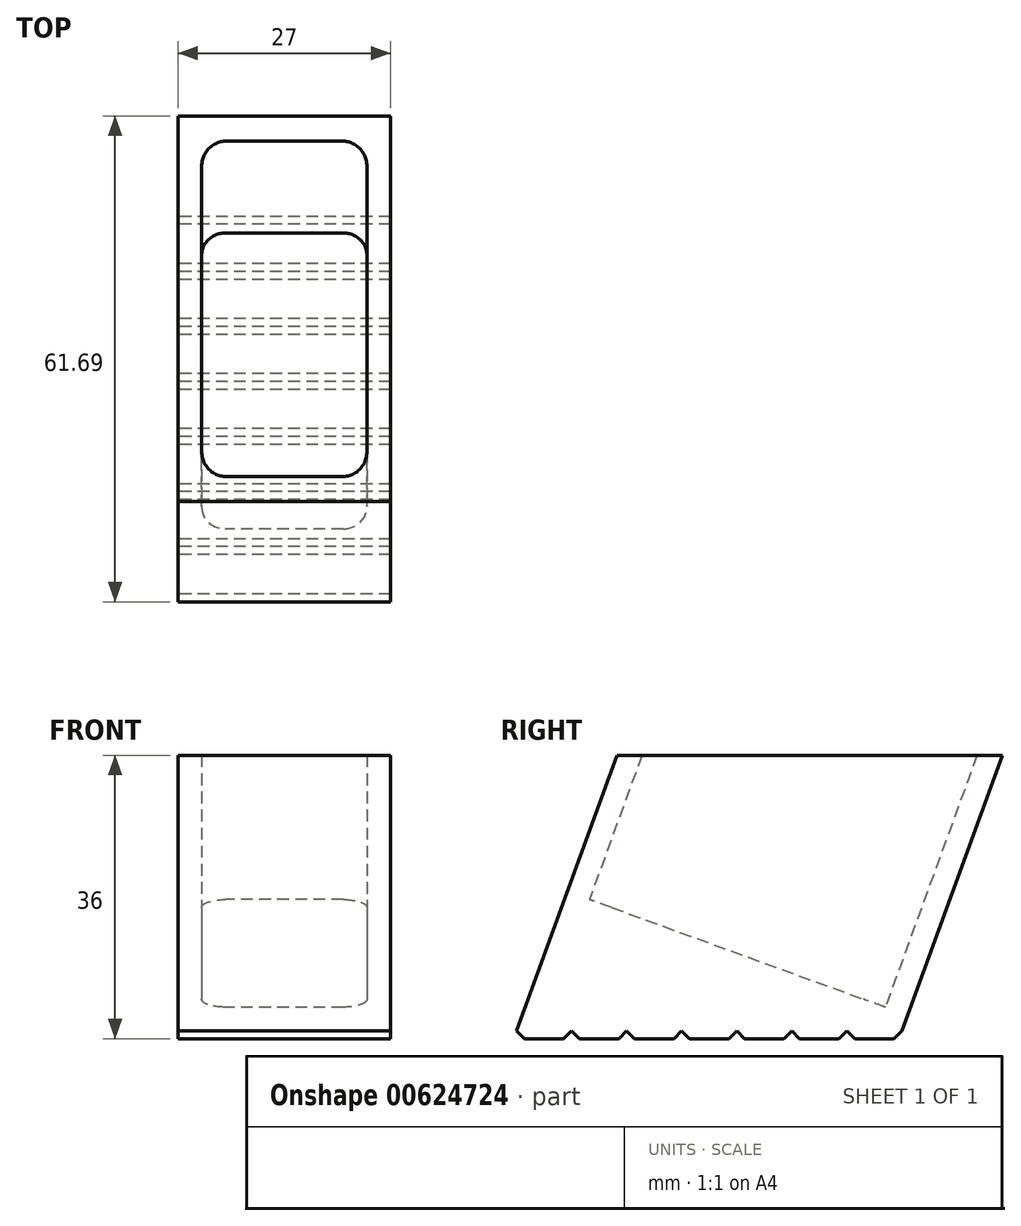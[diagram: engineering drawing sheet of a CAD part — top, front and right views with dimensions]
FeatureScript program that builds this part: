
annotation { "Feature Type Name" : "Feature", "Feature Type Description" : "" }
export const myFeature = defineFeature(function(context is Context, id is Id, definition is map)
    precondition{}
    {
        {
            var Q0;
            Q0=qCreatedBy(makeId("Right.planeOp"),FACE);
            var sketch = newSketch(context, id + "F0", { "sketchPlane" : qUnion([Q0])});
            skLineSegment(sketch, "E0", {"start": v(58.5, 35) * mm, "end": v(46.85, 3) * mm});
            skLineSegment(sketch, "E1", {"start": v(61.7, 35) * mm, "end": v(50.04, 3) * mm});
            skLineSegment(sketch, "E2", {"start": v(15.93, 35) * mm, "end": v(4.28, 3) * mm});
            skLineSegment(sketch, "E3", {"start": v(12.74, 35) * mm, "end": v(1.1, 3) * mm});
            skLineSegment(sketch, "E4", {"start": v(4.28, 3) * mm, "end": v(46.85, 3) * mm});
            skLineSegment(sketch, "E5", {"start": v(50.04, 3) * mm, "end": v(48.95, 0) * mm});
            skLineSegment(sketch, "E6", {"start": v(1.1, 3) * mm, "end": v(0, 0) * mm});
            skLineSegment(sketch, "E7", {"start": v(48.95, 0) * mm, "end": v(0, 0) * mm});
            skLineSegment(sketch, "E8", {"start": v(12.74, 35) * mm, "end": v(15.93, 35) * mm});
            skLineSegment(sketch, "E9", {"start": v(58.5, 35) * mm, "end": v(61.7, 35) * mm});
            skLineSegment(sketch, "E10", {"start": v(9.26, 16.68) * mm, "end": v(46.85, 3) * mm});
            skLineSegment(sketch, "E11", {"start": v(15.93, 35) * mm, "end": v(58.5, 35) * mm});
            skLineSegment(sketch, "E12", {"start": v(0, 0) * mm, "end": v(1, -1) * mm});
            skLineSegment(sketch, "E13", {"start": v(1, -1) * mm, "end": v(6, -1) * mm});
            skLineSegment(sketch, "E14", {"start": v(6, -1) * mm, "end": v(7, 0) * mm});
            skLineSegment(sketch, "E15.1.0.0", {"start": v(7, 0) * mm, "end": v(8, -1) * mm});
            skLineSegment(sketch, "E15.1.0.1", {"start": v(12.99, -1) * mm, "end": v(13.99, 0) * mm});
            skLineSegment(sketch, "E15.1.0.2", {"start": v(8, -1) * mm, "end": v(12.99, -1) * mm});
            skLineSegment(sketch, "E15.2.0.0", {"start": v(13.99, 0) * mm, "end": v(14.99, -1) * mm});
            skLineSegment(sketch, "E15.2.0.1", {"start": v(19.98, -1) * mm, "end": v(20.98, 0) * mm});
            skLineSegment(sketch, "E15.2.0.2", {"start": v(14.99, -1) * mm, "end": v(19.98, -1) * mm});
            skLineSegment(sketch, "E15.3.0.0", {"start": v(20.98, 0) * mm, "end": v(21.98, -1) * mm});
            skLineSegment(sketch, "E15.3.0.1", {"start": v(26.97, -1) * mm, "end": v(27.97, 0) * mm});
            skLineSegment(sketch, "E15.3.0.2", {"start": v(21.98, -1) * mm, "end": v(26.97, -1) * mm});
            skLineSegment(sketch, "E15.4.0.0", {"start": v(27.97, 0) * mm, "end": v(28.97, -1) * mm});
            skLineSegment(sketch, "E15.4.0.1", {"start": v(33.97, -1) * mm, "end": v(34.97, 0) * mm});
            skLineSegment(sketch, "E15.4.0.2", {"start": v(28.97, -1) * mm, "end": v(33.97, -1) * mm});
            skLineSegment(sketch, "E15.5.0.0", {"start": v(34.97, 0) * mm, "end": v(35.97, -1) * mm});
            skLineSegment(sketch, "E15.5.0.1", {"start": v(40.96, -1) * mm, "end": v(41.96, 0) * mm});
            skLineSegment(sketch, "E15.5.0.2", {"start": v(35.97, -1) * mm, "end": v(40.96, -1) * mm});
            skLineSegment(sketch, "E15.6.0.0", {"start": v(41.96, 0) * mm, "end": v(42.96, -1) * mm});
            skLineSegment(sketch, "E15.6.0.1", {"start": v(47.95, -1) * mm, "end": v(48.95, 0) * mm});
            skLineSegment(sketch, "E15.6.0.2", {"start": v(42.96, -1) * mm, "end": v(47.95, -1) * mm});
            skLineSegment(sketch, "E15.direction1", {"start": v(1, -1) * mm, "end": v(8, -1) * mm, "construction": true});
            skSolve(sketch);
        }
        {
            var Q0;
            Q0=makeQuery(id+"F0.imprint","IMPRINT",FACE,{"disambiguationData":[TD([[makeQuery(id+"F0.imprint","IMPRINT",EDGE,{"derivedFrom":sQuery(id+"F0.wireOp",EDGE,"E0")}),1.0]])]});
            var Q1;
            {var subQ0=sQuery(id+"F0.wireOp",EDGE,"E4");Q1=makeQuery(id+"F0.imprint","IMPRINT",FACE,{"disambiguationData":[TD([[makeQuery(id+"F0.imprint","IMPRINT",EDGE,{"derivedFrom":subQ0}),1.0]])]});}
            var Q2;
            Q2=makeQuery(id+"F0.imprint","IMPRINT",FACE,{"disambiguationData":[TD([[makeQuery(id+"F0.imprint","IMPRINT",EDGE,{"derivedFrom":sQuery(id+"F0.wireOp",EDGE,"E0")}),-1.0]])]});
            var Q3;
            {var subQ0=sQuery(id+"F0.wireOp",EDGE,"E12");Q3=makeQuery(id+"F0.imprint","IMPRINT",FACE,{"disambiguationData":[TD([[makeQuery(id+"F0.imprint","IMPRINT",EDGE,{"derivedFrom":subQ0}),1.0]])]});}
            var Q4;
            {var subQ0=sQuery(id+"F0.wireOp",EDGE,"E15.1.0.0");Q4=makeQuery(id+"F0.imprint","IMPRINT",FACE,{"disambiguationData":[TD([[makeQuery(id+"F0.imprint","IMPRINT",EDGE,{"derivedFrom":subQ0}),1.0]])]});}
            var Q5;
            {var subQ0=sQuery(id+"F0.wireOp",EDGE,"E15.2.0.0");Q5=makeQuery(id+"F0.imprint","IMPRINT",FACE,{"disambiguationData":[TD([[makeQuery(id+"F0.imprint","IMPRINT",EDGE,{"derivedFrom":subQ0}),1.0]])]});}
            var Q6;
            {var subQ0=sQuery(id+"F0.wireOp",EDGE,"E15.3.0.0");Q6=makeQuery(id+"F0.imprint","IMPRINT",FACE,{"disambiguationData":[TD([[makeQuery(id+"F0.imprint","IMPRINT",EDGE,{"derivedFrom":subQ0}),1.0]])]});}
            var Q7;
            {var subQ0=sQuery(id+"F0.wireOp",EDGE,"E15.4.0.0");Q7=makeQuery(id+"F0.imprint","IMPRINT",FACE,{"disambiguationData":[TD([[makeQuery(id+"F0.imprint","IMPRINT",EDGE,{"derivedFrom":subQ0}),1.0]])]});}
            var Q8;
            {var subQ0=sQuery(id+"F0.wireOp",EDGE,"E15.5.0.0");Q8=makeQuery(id+"F0.imprint","IMPRINT",FACE,{"disambiguationData":[TD([[makeQuery(id+"F0.imprint","IMPRINT",EDGE,{"derivedFrom":subQ0}),1.0]])]});}
            var Q9;
            {var subQ0=sQuery(id+"F0.wireOp",EDGE,"E15.6.0.0");Q9=makeQuery(id+"F0.imprint","IMPRINT",FACE,{"disambiguationData":[TD([[makeQuery(id+"F0.imprint","IMPRINT",EDGE,{"derivedFrom":subQ0}),1.0]])]});}
            extrude(context, id + "F1", {"entities" : qUnion([Q0, Q1, Q2, Q3, Q4, Q5, Q6, Q7, Q8, Q9]), "depth" : 27 * mm, "offsetDistance" : 25 * mm});
        }
        {
            var Q0;
            Q0=makeQuery(id+"F0.imprint","IMPRINT",FACE,{"disambiguationData":[TD([[makeQuery(id+"F0.imprint","IMPRINT",EDGE,{"derivedFrom":sQuery(id+"F0.wireOp",EDGE,"E0")}),-1.0]])]});
            extrude(context, id + "F2", {"entities" : qUnion([Q0]), "operationType" : NewBodyOperationType.REMOVE, "depth" : 24 * mm, "offsetDistance" : 25 * mm, "hasSecondDirection" : true, "secondDirectionOppositeDirection" : false, "secondDirectionDepth" : 3 * mm});
        }
        {
            var Q0;
            Q0=makeQuery(id+"F2.boolean.opBoolean","COPY",EDGE,{"derivedFrom":makeQuery(id+"F2.opExtrude","CAP_EDGE",EDGE,{"disambiguationData":[OSD([sQuery(id+"F0.wireOp",EDGE,"E2")])],"isStart":true})});
            var Q1;
            Q1=makeQuery(id+"F2.boolean.opBoolean","COPY",EDGE,{"derivedFrom":makeQuery(id+"F2.opExtrude","CAP_EDGE",EDGE,{"disambiguationData":[OSD([sQuery(id+"F0.wireOp",EDGE,"E2")])],"isStart":false})});
            var Q2;
            Q2=makeQuery(id+"F2.boolean.opBoolean","COPY",EDGE,{"derivedFrom":makeQuery(id+"F2.opExtrude","CAP_EDGE",EDGE,{"disambiguationData":[OSD([sQuery(id+"F0.wireOp",EDGE,"E0")])],"isStart":false})});
            var Q3;
            Q3=makeQuery(id+"F2.boolean.opBoolean","COPY",EDGE,{"derivedFrom":makeQuery(id+"F2.opExtrude","CAP_EDGE",EDGE,{"disambiguationData":[OSD([sQuery(id+"F0.wireOp",EDGE,"E0")])],"isStart":true})});
            fillet(context, id + "F3", {"entities" : qUnion([Q0, Q1, Q2, Q3]), "radius" : 3 * mm, "tangentPropagation" : true, "allowEdgeOverflow" : false});
        }
    });
